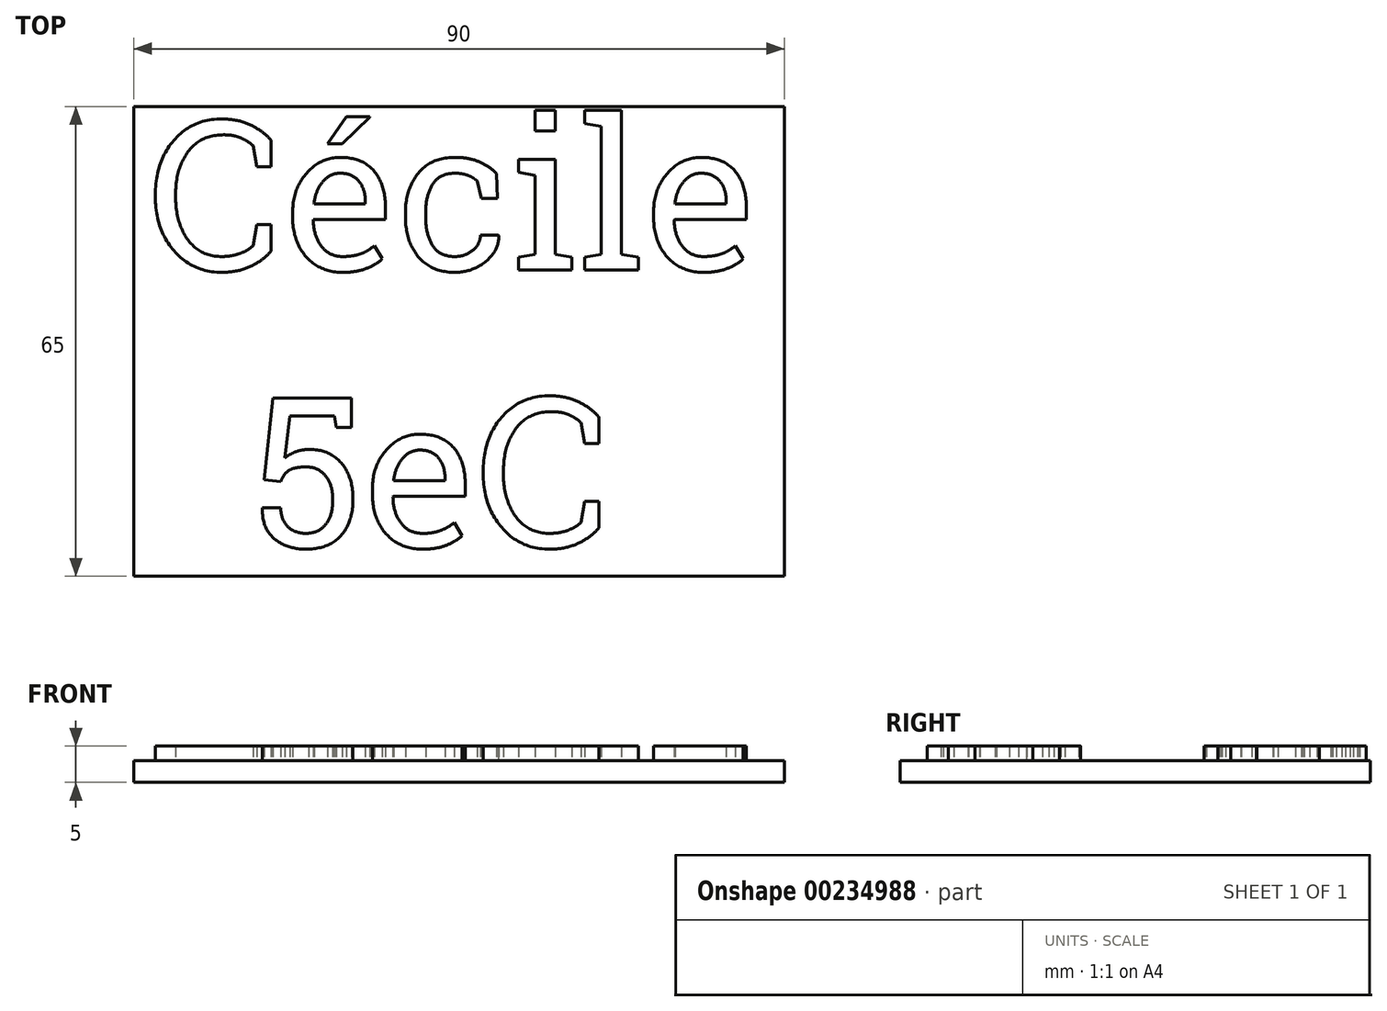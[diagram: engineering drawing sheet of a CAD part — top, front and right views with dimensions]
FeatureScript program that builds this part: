
annotation { "Feature Type Name" : "Feature", "Feature Type Description" : "" }
export const myFeature = defineFeature(function(context is Context, id is Id, definition is map)
    precondition{}
    {
        {
            var Q0;
            Q0=qCreatedBy(makeId("Top.planeOp"),FACE);
            var sketch = newSketch(context, id + "F0", { "sketchPlane" : qUnion([Q0])});
            skLineSegment(sketch, "E0.bottom", {"start": v(0, 0) * mm, "end": v(90, 0) * mm});
            skLineSegment(sketch, "E0.top", {"start": v(0, -65) * mm, "end": v(90, -65) * mm});
            skLineSegment(sketch, "E0.left", {"start": v(0, 0) * mm, "end": v(0, -65) * mm});
            skLineSegment(sketch, "E0.right", {"start": v(90, 0) * mm, "end": v(90, -65) * mm});
            skSolve(sketch);
        }
        {
            var Q0;
            Q0=makeQuery(id+"F0.imprint","IMPRINT",FACE,{"disambiguationData":[TD([[makeQuery(id+"F0.imprint","IMPRINT",EDGE,{"derivedFrom":sQuery(id+"F0.wireOp",EDGE,"E0.bottom")}),-1.0]])]});
            extrude(context, id + "F1", {"entities" : qUnion([Q0]), "depth" : 3 * mm});
        }
        {
            var Q0;
            Q0=makeQuery(id+"F1.opExtrude","CAP_FACE",FACE,{"disambiguationData":[OSD([sQuery(id+"F0.wireOp",EDGE,"E0.bottom"),sQuery(id+"F0.wireOp",EDGE,"E0.top"),sQuery(id+"F0.wireOp",EDGE,"E0.left"),sQuery(id+"F0.wireOp",EDGE,"E0.right")])],"isStart":false});
            var sketch = newSketch(context, id + "F2", { "sketchPlane" : qUnion([Q0])});
            skText(sketch, "E1", { "text": "Cécile\n  5eC", "fontName": "RobotoSlab-Regular.ttf"});
            const initialGuessF2  = {"E1": [0.002, -0.02265, 1, 0, 0.02089]};
            skSetInitialGuess(sketch, initialGuessF2);
            skSolve(sketch);
        }
        {
            var Q0;
            Q0 = qSketchRegion(id + "F2", true);
            extrude(context, id + "F3", {"entities" : qUnion([Q0]), "operationType" : NewBodyOperationType.ADD, "depth" : 2 * mm});
        }
    });
